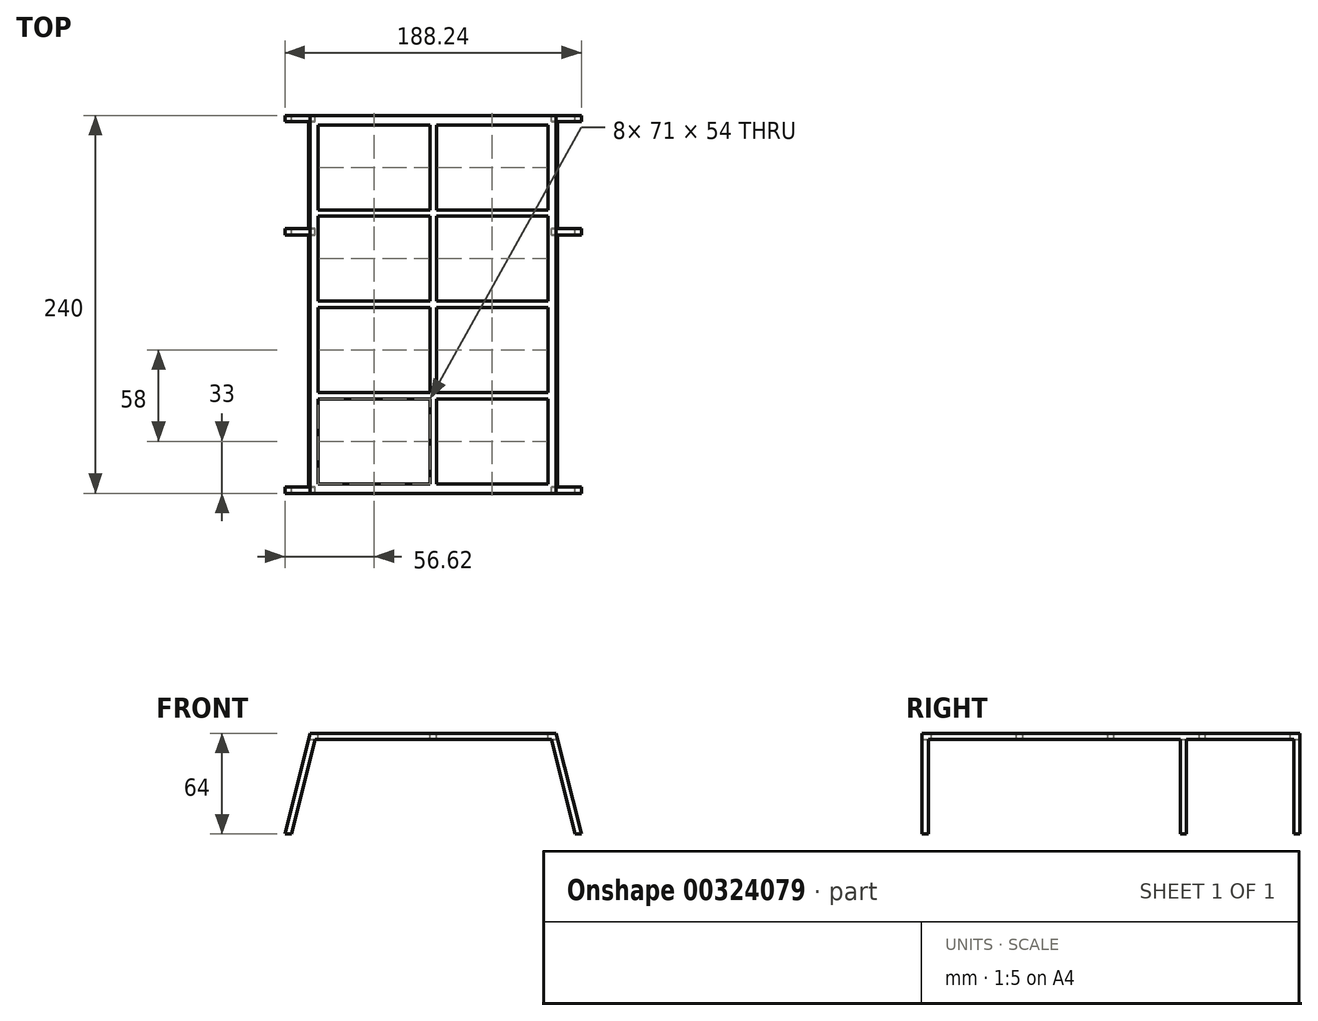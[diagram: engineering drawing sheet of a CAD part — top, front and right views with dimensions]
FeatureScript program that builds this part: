
annotation { "Feature Type Name" : "Feature", "Feature Type Description" : "" }
export const myFeature = defineFeature(function(context is Context, id is Id, definition is map)
    precondition{}
    {
        {
            var Q0;
            Q0=qCreatedBy(makeId("Front.planeOp"),FACE);
            var sketch = newSketch(context, id + "F0", { "sketchPlane" : qUnion([Q0])});
            skLineSegment(sketch, "E0", {"start": v(-90, 0) * mm, "end": v(-75, 60) * mm});
            skLineSegment(sketch, "E1", {"start": v(-75, 60) * mm, "end": v(75, 60) * mm});
            skLineSegment(sketch, "E2", {"start": v(75, 60) * mm, "end": v(90, 0) * mm});
            skLineSegment(sketch, "E3", {"start": v(-94.12, 0) * mm, "end": v(-78.12, 64) * mm});
            skLineSegment(sketch, "E4", {"start": v(-78.12, 64) * mm, "end": v(78.12, 64) * mm});
            skLineSegment(sketch, "E5", {"start": v(78.12, 64) * mm, "end": v(94.12, 0) * mm});
            skLineSegment(sketch, "E6", {"start": v(-94.12, 0) * mm, "end": v(-90, 0) * mm});
            skLineSegment(sketch, "E7", {"start": v(90, 0) * mm, "end": v(94.12, 0) * mm});
            skLineSegment(sketch, "E8", {"start": v(0, 0) * mm, "end": v(0, 60) * mm, "construction": true});
            skSolve(sketch);
        }
        {
            var Q0;
            Q0=makeQuery(id+"F0.imprint","IMPRINT",FACE,{"disambiguationData":[TD([[makeQuery(id+"F0.imprint","IMPRINT",EDGE,{"derivedFrom":sQuery(id+"F0.wireOp",EDGE,"E0")}),1.0]])]});
            extrude(context, id + "F1", {"entities" : qUnion([Q0]), "endBound" : BoundingType.SYMMETRIC, "depth" : 240 * mm});
        }
        {
            var Q0;
            Q0=qCreatedBy(makeId("Right.planeOp"),FACE);
            var sketch = newSketch(context, id + "F2", { "sketchPlane" : qUnion([Q0])});
            skLineSegment(sketch, "E9.bottom", {"start": v(-116, 0) * mm, "end": v(44, 0) * mm});
            skLineSegment(sketch, "E9.top", {"start": v(-116, 60) * mm, "end": v(44, 60) * mm});
            skLineSegment(sketch, "E9.left", {"start": v(-116, 0) * mm, "end": v(-116, 60) * mm});
            skLineSegment(sketch, "E9.right", {"start": v(44, 0) * mm, "end": v(44, 60) * mm});
            skLineSegment(sketch, "E10.bottom", {"start": v(48, 0) * mm, "end": v(116, 0) * mm});
            skLineSegment(sketch, "E10.top", {"start": v(48, 60) * mm, "end": v(116, 60) * mm});
            skLineSegment(sketch, "E10.left", {"start": v(48, 0) * mm, "end": v(48, 60) * mm});
            skLineSegment(sketch, "E10.right", {"start": v(116, 0) * mm, "end": v(116, 60) * mm});
            skSolve(sketch);
        }
        {
            var Q0;
            Q0=makeQuery(id+"F2.imprint","IMPRINT",FACE,{"disambiguationData":[TD([[makeQuery(id+"F2.imprint","IMPRINT",EDGE,{"derivedFrom":sQuery(id+"F2.wireOp",EDGE,"E9.bottom")}),1.0]])]});
            var Q1;
            Q1=makeQuery(id+"F2.imprint","IMPRINT",FACE,{"disambiguationData":[TD([[makeQuery(id+"F2.imprint","IMPRINT",EDGE,{"derivedFrom":sQuery(id+"F2.wireOp",EDGE,"E10.bottom")}),1.0]])]});
            extrude(context, id + "F3", {"entities" : qUnion([Q0, Q1]), "operationType" : NewBodyOperationType.REMOVE, "endBound" : BoundingType.SYMMETRIC, "oppositeDirection" : true, "depth" : 200 * mm});
        }
        {
            var Q0;
            Q0=makeQuery(id+"F1.opExtrude","SWEPT_FACE",FACE,{"disambiguationData":[OSD([sQuery(id+"F0.wireOp",EDGE,"E4")])]});
            var sketch = newSketch(context, id + "F4", { "sketchPlane" : qUnion([Q0])});
            skLineSegment(sketch, "E11.bottom", {"start": v(-73, 114) * mm, "end": v(-2, 114) * mm});
            skLineSegment(sketch, "E11.top", {"start": v(-73, 60) * mm, "end": v(-2, 60) * mm});
            skLineSegment(sketch, "E11.left", {"start": v(-73, 114) * mm, "end": v(-73, 60) * mm});
            skLineSegment(sketch, "E11.right", {"start": v(-2, 114) * mm, "end": v(-2, 60) * mm});
            skLineSegment(sketch, "E12.bottom", {"start": v(-73, 56) * mm, "end": v(-2, 56) * mm});
            skLineSegment(sketch, "E12.top", {"start": v(-73, 2) * mm, "end": v(-2, 2) * mm});
            skLineSegment(sketch, "E12.left", {"start": v(-73, 56) * mm, "end": v(-73, 2) * mm});
            skLineSegment(sketch, "E12.right", {"start": v(-2, 56) * mm, "end": v(-2, 2) * mm});
            skLineSegment(sketch, "E13", {"start": v(0, 0) * mm, "end": v(0, 17.51) * mm, "construction": true});
            skLineSegment(sketch, "E14.MirrorCS", {"start": v(73, 2) * mm, "end": v(2, 2) * mm});
            skLineSegment(sketch, "E15.MirrorCS", {"start": v(2, 56) * mm, "end": v(2, 2) * mm});
            skLineSegment(sketch, "E16.MirrorCS", {"start": v(73, 56) * mm, "end": v(73, 2) * mm});
            skLineSegment(sketch, "E17.MirrorCS", {"start": v(73, 56) * mm, "end": v(2, 56) * mm});
            skLineSegment(sketch, "E18.MirrorCS", {"start": v(73, 60) * mm, "end": v(2, 60) * mm});
            skLineSegment(sketch, "E19.MirrorCS", {"start": v(2, 114) * mm, "end": v(2, 60) * mm});
            skLineSegment(sketch, "E20.MirrorCS", {"start": v(73, 114) * mm, "end": v(73, 60) * mm});
            skLineSegment(sketch, "E21.MirrorCS", {"start": v(73, 114) * mm, "end": v(2, 114) * mm});
            skLineSegment(sketch, "E22", {"start": v(-16.33, 0) * mm, "end": v(18.12, 0) * mm, "construction": true});
            skLineSegment(sketch, "E23.MirrorCS", {"start": v(73, -2) * mm, "end": v(2, -2) * mm});
            skLineSegment(sketch, "E24.MirrorCS", {"start": v(-2, -56) * mm, "end": v(-2, -2) * mm});
            skLineSegment(sketch, "E25.MirrorCS", {"start": v(-73, -2) * mm, "end": v(-2, -2) * mm});
            skLineSegment(sketch, "E26.MirrorCS", {"start": v(2, -56) * mm, "end": v(2, -2) * mm});
            skLineSegment(sketch, "E27.MirrorCS", {"start": v(-73, -56) * mm, "end": v(-73, -2) * mm});
            skLineSegment(sketch, "E28.MirrorCS", {"start": v(-73, -60) * mm, "end": v(-2, -60) * mm});
            skLineSegment(sketch, "E29.MirrorCS", {"start": v(-73, -56) * mm, "end": v(-2, -56) * mm});
            skLineSegment(sketch, "E30.MirrorCS", {"start": v(73, -60) * mm, "end": v(2, -60) * mm});
            skLineSegment(sketch, "E31.MirrorCS", {"start": v(73, -114) * mm, "end": v(73, -60) * mm});
            skLineSegment(sketch, "E32.MirrorCS", {"start": v(73, -56) * mm, "end": v(2, -56) * mm});
            skLineSegment(sketch, "E33.MirrorCS", {"start": v(73, -56) * mm, "end": v(73, -2) * mm});
            skLineSegment(sketch, "E34.MirrorCS", {"start": v(2, -114) * mm, "end": v(2, -60) * mm});
            skLineSegment(sketch, "E35.MirrorCS", {"start": v(-2, -114) * mm, "end": v(-2, -60) * mm});
            skLineSegment(sketch, "E36.MirrorCS", {"start": v(-73, -114) * mm, "end": v(-73, -60) * mm});
            skLineSegment(sketch, "E37.MirrorCS", {"start": v(-73, -114) * mm, "end": v(-2, -114) * mm});
            skLineSegment(sketch, "E38.MirrorCS", {"start": v(73, -114) * mm, "end": v(2, -114) * mm});
            skSolve(sketch);
        }
        {
            var Q0;
            Q0=makeQuery(id+"F4.imprint","IMPRINT",FACE,{"disambiguationData":[TD([[makeQuery(id+"F4.imprint","IMPRINT",EDGE,{"derivedFrom":sQuery(id+"F4.wireOp",EDGE,"E11.bottom")}),-1.0]])]});
            var Q1;
            Q1=makeQuery(id+"F4.imprint","IMPRINT",FACE,{"disambiguationData":[TD([[makeQuery(id+"F4.imprint","IMPRINT",EDGE,{"derivedFrom":sQuery(id+"F4.wireOp",EDGE,"E18.MirrorCS")}),-1.0]])]});
            var Q2;
            Q2=makeQuery(id+"F4.imprint","IMPRINT",FACE,{"disambiguationData":[TD([[makeQuery(id+"F4.imprint","IMPRINT",EDGE,{"derivedFrom":sQuery(id+"F4.wireOp",EDGE,"E12.bottom")}),-1.0]])]});
            var Q3;
            Q3=makeQuery(id+"F4.imprint","IMPRINT",FACE,{"disambiguationData":[TD([[makeQuery(id+"F4.imprint","IMPRINT",EDGE,{"derivedFrom":sQuery(id+"F4.wireOp",EDGE,"E14.MirrorCS")}),-1.0]])]});
            var Q4;
            Q4=makeQuery(id+"F4.imprint","IMPRINT",FACE,{"disambiguationData":[TD([[makeQuery(id+"F4.imprint","IMPRINT",EDGE,{"derivedFrom":sQuery(id+"F4.wireOp",EDGE,"E24.MirrorCS")}),1.0]])]});
            var Q5;
            Q5=makeQuery(id+"F4.imprint","IMPRINT",FACE,{"disambiguationData":[TD([[makeQuery(id+"F4.imprint","IMPRINT",EDGE,{"derivedFrom":sQuery(id+"F4.wireOp",EDGE,"E23.MirrorCS")}),1.0]])]});
            var Q6;
            Q6=makeQuery(id+"F4.imprint","IMPRINT",FACE,{"disambiguationData":[TD([[makeQuery(id+"F4.imprint","IMPRINT",EDGE,{"derivedFrom":sQuery(id+"F4.wireOp",EDGE,"E28.MirrorCS")}),-1.0]])]});
            var Q7;
            Q7=makeQuery(id+"F4.imprint","IMPRINT",FACE,{"disambiguationData":[TD([[makeQuery(id+"F4.imprint","IMPRINT",EDGE,{"derivedFrom":sQuery(id+"F4.wireOp",EDGE,"E30.MirrorCS")}),1.0]])]});
            extrude(context, id + "F5", {"entities" : qUnion([Q0, Q1, Q2, Q3, Q4, Q5, Q6, Q7]), "operationType" : NewBodyOperationType.REMOVE, "oppositeDirection" : true, "depth" : 80.36 * mm});
        }
    });
